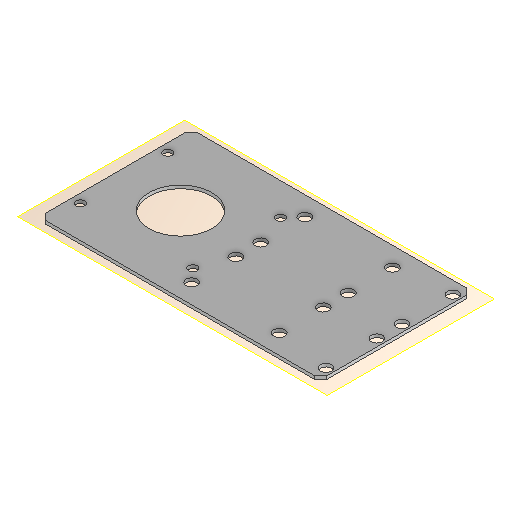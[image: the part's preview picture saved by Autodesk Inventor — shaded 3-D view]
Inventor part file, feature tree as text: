
AUTODESK INVENTOR PART (.ipt)
format: ipt  version: 2024.1 (Build 281209000, 209)  size: 124,928 bytes
history: native  units: mm
features: other x2, plane x1, extrude x1, sketch x1, reference x1
ambient origin geometry x8: Origin, YZ Plane, XZ Plane, XY Plane, X Axis, Y Axis, Z Axis, Center Point
bodies: Volumenkörper1 (feature_tree)
feature tree (6):
  plane  "Arbeitsebene1"
  extrude  "Extrusion1"  [1 undecoded]
  sketch  "Skizze1"  dims[d0=1.0mm d1=0.0mm]
  reference  "Referenz1"
  other  "Assembly_Planktoscope_Uc2version_wormdrive_V3.iam"
  other  "60_Planktoscope_Sampleholder:1"
note: 1 required parameter value undecoded (feature->parameter linkage not recoverable at this tier; creation-order binding heuristic only, values carry confidence <= 0.55)
